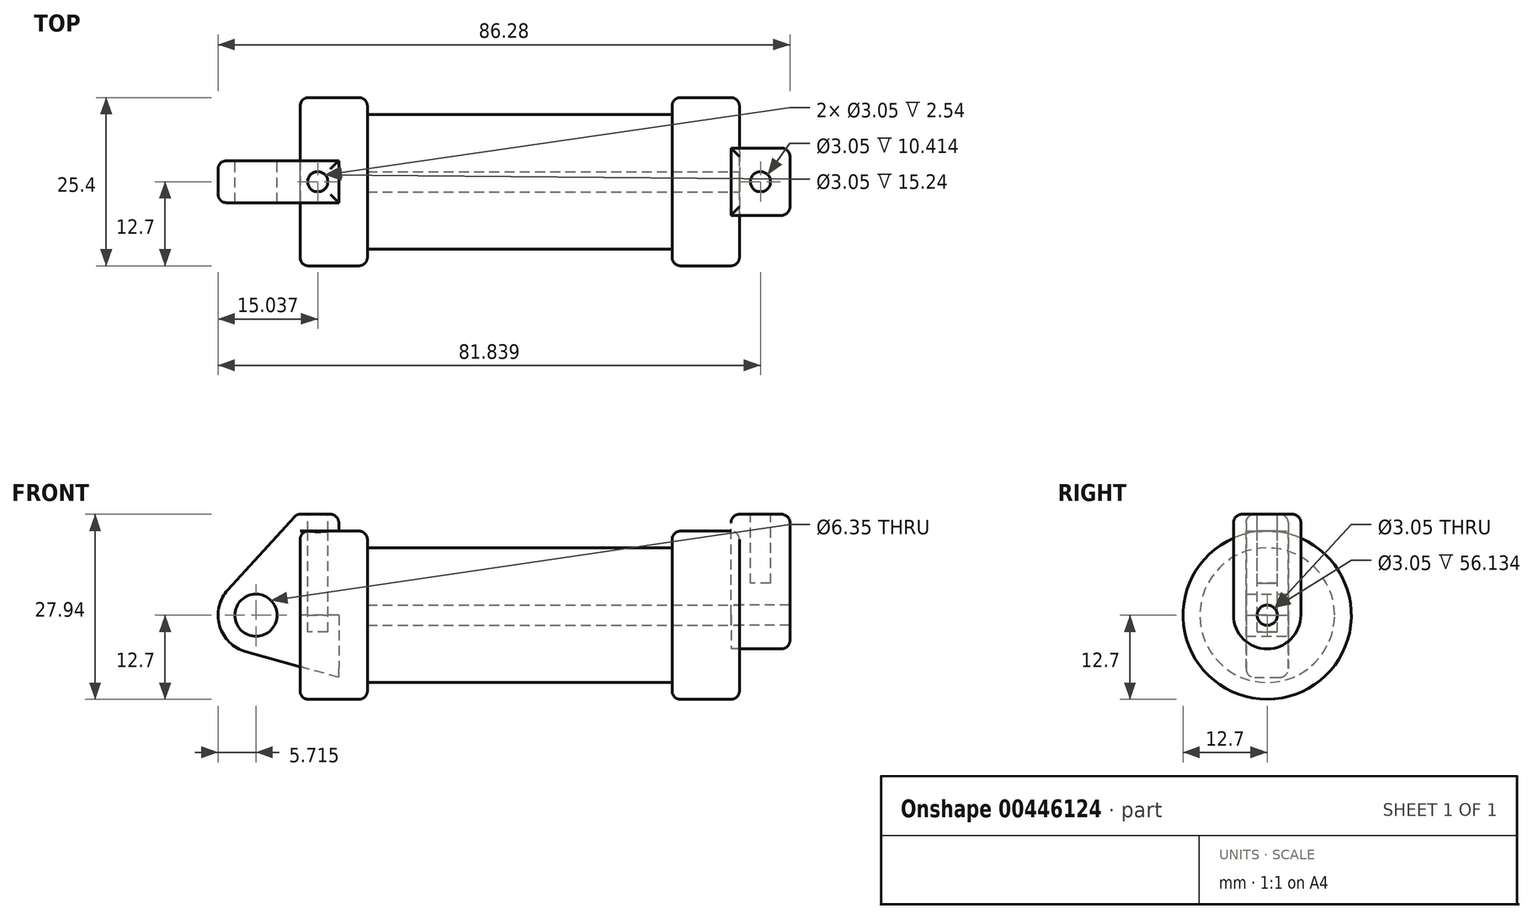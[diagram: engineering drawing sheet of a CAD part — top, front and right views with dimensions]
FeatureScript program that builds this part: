
annotation { "Feature Type Name" : "Feature", "Feature Type Description" : "" }
export const myFeature = defineFeature(function(context is Context, id is Id, definition is map)
    precondition{}
    {
        {
            var Q0;
            Q0=qCreatedBy(makeId("Front.planeOp"),FACE);
            var sketch = newSketch(context, id + "F0", { "sketchPlane" : qUnion([Q0])});
            skLineSegment(sketch, "E0", {"start": v(0, 0) * mm, "end": v(0, 12.7) * mm});
            skLineSegment(sketch, "E1", {"start": v(0, 12.7) * mm, "end": v(10.16, 12.7) * mm});
            skLineSegment(sketch, "E2", {"start": v(10.16, 12.7) * mm, "end": v(10.16, 10.16) * mm});
            skLineSegment(sketch, "E3", {"start": v(10.16, 10.16) * mm, "end": v(56.13, 10.16) * mm});
            skLineSegment(sketch, "E4", {"start": v(56.13, 10.16) * mm, "end": v(56.13, 12.7) * mm});
            skLineSegment(sketch, "E5", {"start": v(56.13, 12.7) * mm, "end": v(66.3, 12.7) * mm});
            skLineSegment(sketch, "E6", {"start": v(66.3, 12.7) * mm, "end": v(66.3, 0) * mm});
            skLineSegment(sketch, "E7", {"start": v(66.3, 0) * mm, "end": v(0, 0) * mm});
            skLineSegment(sketch, "E8", {"start": v(5.84, 15.24) * mm, "end": v(-0.5, 15.24) * mm});
            skLineSegment(sketch, "E9", {"start": v(-0.5, 15.24) * mm, "end": v(-10.88, 3.85) * mm});
            skLineSegment(sketch, "E10", {"start": v(0, 0) * mm, "end": v(-6.65, 0) * mm});
            skCircle(sketch, "E11", {"center": v(-6.65, 0) * mm, "radius": 5.72 * mm});
            skCircle(sketch, "E12", {"center": v(-6.65, 0) * mm, "radius": 3.18 * mm});
            skLineSegment(sketch, "E13", {"start": v(5.84, 15.24) * mm, "end": v(5.84, -9.4) * mm});
            skLineSegment(sketch, "E14", {"start": v(5.84, -9.4) * mm, "end": v(-8.18, -5.5) * mm});
            skSolve(sketch);
        }
        {
            var Q0;
            {var subQ0=sQuery(id+"F0.wireOp",EDGE,"E2");Q0=makeQuery(id+"F0.imprint","IMPRINT",FACE,{"disambiguationData":[TD([[makeQuery(id+"F0.imprint","IMPRINT",EDGE,{"derivedFrom":subQ0}),-1.0]])]});}
            var Q1;
            {var subQ0=sQuery(id+"F0.wireOp",EDGE,"E0");Q1=makeQuery(id+"F0.imprint","IMPRINT",FACE,{"disambiguationData":[TD([[makeQuery(id+"F0.imprint","IMPRINT",EDGE,{"derivedFrom":subQ0}),-1.0]])]});}
            var Q2;
            Q2=sQuery(id+"F0.wireOp",EDGE,"E7");
            revolve(context, id + "F1", {"entities" : qUnion([Q0, Q1]), "axis" : qUnion([Q2]), "revolveType" : RevolveType.FULL});
        }
        {
            var Q0;
            {var subQ1=sQuery(id+"F0.wireOp",EDGE,"E0");Q0=makeQuery(id+"F0.imprint","IMPRINT",FACE,{"disambiguationData":[TD([[makeQuery(id+"F0.imprint","IMPRINT",EDGE,{"derivedFrom":subQ1}),1.0]])]});}
            var Q1;
            {var subQ5=sQuery(id+"F0.wireOp",EDGE,"E12");Q1=makeQuery(id+"F0.imprint","IMPRINT",FACE,{"disambiguationData":[TD([[makeQuery(id+"F0.imprint","IMPRINT",EDGE,{"derivedFrom":subQ5}),-1.0]])]});}
            var Q2;
            {var subQ0=sQuery(id+"F0.wireOp",EDGE,"E14");Q2=makeQuery(id+"F0.imprint","IMPRINT",FACE,{"disambiguationData":[TD([[makeQuery(id+"F0.imprint","IMPRINT",EDGE,{"derivedFrom":subQ0}),-1.0]])]});}
            extrude(context, id + "F2", {"entities" : qUnion([Q0, Q1, Q2]), "endBound" : BoundingType.SYMMETRIC, "depth" : 6.35 * mm});
        }
        {
            var Q0;
            Q0=makeQuery(id+"F1.opRevolve","SWEPT_FACE",FACE,{"disambiguationData":[OSD([sQuery(id+"F0.wireOp",EDGE,"E6")])]});
            var sketch = newSketch(context, id + "F3", { "sketchPlane" : qUnion([Q0])});
            skCircle(sketch, "E15", {"center": v(0, 0) * mm, "radius": 1.52 * mm});
            skCircle(sketch, "E16", {"center": v(0, 0) * mm, "radius": 5.08 * mm});
            skLineSegment(sketch, "E17.top", {"start": v(5.08, 15.24) * mm, "end": v(-5.08, 15.24) * mm});
            skLineSegment(sketch, "E17.left", {"start": v(5.08, 0) * mm, "end": v(5.08, 15.24) * mm});
            skLineSegment(sketch, "E17.right", {"start": v(-5.08, 0) * mm, "end": v(-5.08, 15.24) * mm});
            skSolve(sketch);
        }
        {
            var Q0;
            Q0 = qSketchRegion(id + "F3", true);
            extrude(context, id + "F4", {"entities" : qUnion([Q0]), "depth" : 7.62 * mm, "hasSecondDirection" : true, "secondDirectionOppositeDirection" : true, "secondDirectionDepth" : 1.27 * mm});
        }
        {
            var Q0;
            Q0=makeQuery(id+"F4.opExtrude","CAP_FACE",FACE,{"disambiguationData":[OSD([sQuery(id+"F3.wireOp",EDGE,"E15"),sQuery(id+"F3.wireOp",EDGE,"E16"),sQuery(id+"F3.wireOp",EDGE,"E17.top"),sQuery(id+"F3.wireOp",EDGE,"E17.left"),sQuery(id+"F3.wireOp",EDGE,"E17.right")])],"isStart":false});
            var sketch = newSketch(context, id + "F5", { "sketchPlane" : qUnion([Q0])});
            skCircle(sketch, "E18", {"center": v(0, 0) * mm, "radius": 1.52 * mm});
            skSolve(sketch);
        }
        {
            var Q0;
            Q0 = qSketchRegion(id + "F5", true);
            var Q1;
            Q1=makeQuery(id+"F1.opRevolve","SWEPT_FACE",FACE,{"disambiguationData":[OSD([sQuery(id+"F0.wireOp",EDGE,"E2")])]});
            extrude(context, id + "F6", {"entities" : qUnion([Q0]), "operationType" : NewBodyOperationType.REMOVE, "endBound" : BoundingType.UP_TO_SURFACE, "oppositeDirection" : true, "endBoundEntityFace" : qUnion([Q1]), "depth" : 25.4 * mm});
        }
        {
            var Q0;
            Q0=makeQuery(id+"F4.opExtrude","SWEPT_FACE",FACE,{"disambiguationData":[OSD([sQuery(id+"F3.wireOp",EDGE,"E17.top")])]});
            var sketch = newSketch(context, id + "F7", { "sketchPlane" : qUnion([Q0])});
            skPoint(sketch, "E19", {"position": v(69.47, 5.08) * mm});
            skPoint(sketch, "E20", {"position": v(73.91, 0) * mm});
            skLineSegment(sketch, "E21", {"start": v(73.91, 0) * mm, "end": v(65.02, 0) * mm, "construction": true});
            skLineSegment(sketch, "E22", {"start": v(69.47, 5.08) * mm, "end": v(69.47, -5.08) * mm, "construction": true});
            skCircle(sketch, "E23", {"center": v(69.47, 0) * mm, "radius": 1.52 * mm});
            skSolve(sketch);
        }
        {
            var Q0;
            Q0=makeQuery(id+"F2.opExtrude","SWEPT_FACE",FACE,{"disambiguationData":[OSD([sQuery(id+"F0.wireOp",EDGE,"E8")])]});
            var sketch = newSketch(context, id + "F8", { "sketchPlane" : qUnion([Q0])});
            skLineSegment(sketch, "E24", {"start": v(5.84, 0) * mm, "end": v(-0.5, 0) * mm, "construction": true});
            skLineSegment(sketch, "E25", {"start": v(2.67, -3.18) * mm, "end": v(2.67, 3.18) * mm, "construction": true});
            skCircle(sketch, "E26", {"center": v(2.67, 0) * mm, "radius": 1.52 * mm});
            skSolve(sketch);
        }
        {
            var Q0;
            Q0 = qSketchRegion(id + "F8", true);
            extrude(context, id + "F9", {"entities" : qUnion([Q0]), "operationType" : NewBodyOperationType.REMOVE, "oppositeDirection" : true, "depth" : 17.78 * mm});
        }
        {
            var Q0;
            Q0=makeQuery(id+"F7.imprint","IMPRINT",FACE,{"disambiguationData":[TD([[makeQuery(id+"F7.imprint","IMPRINT",EDGE,{"derivedFrom":sQuery(id+"F7.wireOp",EDGE,"E23")}),1.0]])]});
            extrude(context, id + "F10", {"entities" : qUnion([Q0]), "operationType" : NewBodyOperationType.REMOVE, "oppositeDirection" : true, "depth" : 10.4 * mm});
        }
        {
            var Q0;
            Q0=makeQuery(id+"F1.opRevolve","SWEPT_EDGE",EDGE,{"disambiguationData":[OSD([sQuery(id+"F0.wireOp",EDGE,"E4"),sQuery(id+"F0.wireOp",EDGE,"E5")])]});
            var Q1;
            Q1=makeQuery(id+"F1.opRevolve","SWEPT_EDGE",EDGE,{"disambiguationData":[OSD([sQuery(id+"F0.wireOp",EDGE,"E5"),sQuery(id+"F0.wireOp",EDGE,"E6")])]});
            var Q2;
            Q2=makeQuery(id+"F1.opRevolve","SWEPT_EDGE",EDGE,{"disambiguationData":[OSD([sQuery(id+"F0.wireOp",EDGE,"E1"),sQuery(id+"F0.wireOp",EDGE,"E2")])]});
            var Q3;
            Q3=makeQuery(id+"F1.opRevolve","SWEPT_EDGE",EDGE,{"disambiguationData":[OSD([sQuery(id+"F0.wireOp",EDGE,"E0"),sQuery(id+"F0.wireOp",EDGE,"E1")])]});
            var Q4;
            Q4=makeQuery(id+"F2.opExtrude","SWEPT_EDGE",EDGE,{"disambiguationData":[OSD([sQuery(id+"F0.wireOp",EDGE,"E8"),sQuery(id+"F0.wireOp",EDGE,"E13")])]});
            var Q5;
            Q5=makeQuery(id+"F2.opExtrude","CAP_EDGE",EDGE,{"disambiguationData":[OSD([sQuery(id+"F0.wireOp",EDGE,"E8")])],"isStart":true});
            var Q6;
            Q6=makeQuery(id+"F2.opExtrude","SWEPT_EDGE",EDGE,{"disambiguationData":[OSD([sQuery(id+"F0.wireOp",EDGE,"E8"),sQuery(id+"F0.wireOp",EDGE,"E9")])]});
            var Q7;
            Q7=makeQuery(id+"F2.opExtrude","CAP_EDGE",EDGE,{"disambiguationData":[OSD([sQuery(id+"F0.wireOp",EDGE,"E8")])],"isStart":false});
            var Q8;
            Q8=makeQuery(id+"F4.opExtrude","CAP_EDGE",EDGE,{"disambiguationData":[OSD([sQuery(id+"F3.wireOp",EDGE,"E17.top")])],"isStart":false});
            var Q9;
            Q9=makeQuery(id+"F4.opExtrude","SWEPT_EDGE",EDGE,{"disambiguationData":[OSD([sQuery(id+"F3.wireOp",EDGE,"E17.top"),sQuery(id+"F3.wireOp",EDGE,"E17.right")])]});
            var Q10;
            Q10=makeQuery(id+"F4.opExtrude","CAP_EDGE",EDGE,{"disambiguationData":[OSD([sQuery(id+"F3.wireOp",EDGE,"E17.top")])],"isStart":true});
            var Q11;
            Q11=makeQuery(id+"F4.opExtrude","SWEPT_EDGE",EDGE,{"disambiguationData":[OSD([sQuery(id+"F3.wireOp",EDGE,"E17.top"),sQuery(id+"F3.wireOp",EDGE,"E17.left")])]});
            var Q12;
            Q12=makeQuery(id+"F4.opExtrude","CAP_EDGE",EDGE,{"disambiguationData":[OSD([sQuery(id+"F3.wireOp",EDGE,"E16")])],"isStart":false});
            var Q13;
            Q13=makeQuery(id+"F4.opExtrude","CAP_EDGE",EDGE,{"disambiguationData":[OSD([sQuery(id+"F3.wireOp",EDGE,"E17.left")])],"isStart":false});
            var Q14;
            Q14=makeQuery(id+"F4.opExtrude","CAP_EDGE",EDGE,{"disambiguationData":[OSD([sQuery(id+"F3.wireOp",EDGE,"E17.right")])],"isStart":false});
            var Q15;
            Q15=makeQuery(id+"F2.opExtrude","CAP_EDGE",EDGE,{"disambiguationData":[OSD([sQuery(id+"F0.wireOp",EDGE,"E9")])],"isStart":false});
            var Q16;
            Q16=makeQuery(id+"F2.opExtrude","CAP_EDGE",EDGE,{"disambiguationData":[OSD([sQuery(id+"F0.wireOp",EDGE,"E11")])],"isStart":false});
            var Q17;
            Q17=makeQuery(id+"F2.opExtrude","CAP_EDGE",EDGE,{"disambiguationData":[OSD([sQuery(id+"F0.wireOp",EDGE,"E11")])],"isStart":true});
            var Q18;
            Q18=makeQuery(id+"F2.opExtrude","CAP_EDGE",EDGE,{"disambiguationData":[OSD([sQuery(id+"F0.wireOp",EDGE,"E9")])],"isStart":true});
            var Q19;
            Q19=makeQuery(id+"F2.opExtrude","CAP_EDGE",EDGE,{"disambiguationData":[OSD([sQuery(id+"F0.wireOp",EDGE,"E14")])],"isStart":false});
            var Q20;
            Q20=makeQuery(id+"F2.opExtrude","CAP_EDGE",EDGE,{"disambiguationData":[OSD([sQuery(id+"F0.wireOp",EDGE,"E14")])],"isStart":true});
            fillet(context, id + "F11", {"entities" : qUnion([Q0, Q1, Q2, Q3, Q4, Q5, Q6, Q7, Q8, Q9, Q10, Q11, Q12, Q13, Q14, Q15, Q16, Q17, Q18, Q19, Q20]), "radius" : 1.27 * mm, "tangentPropagation" : true, "allowEdgeOverflow" : false});
        }
    });
